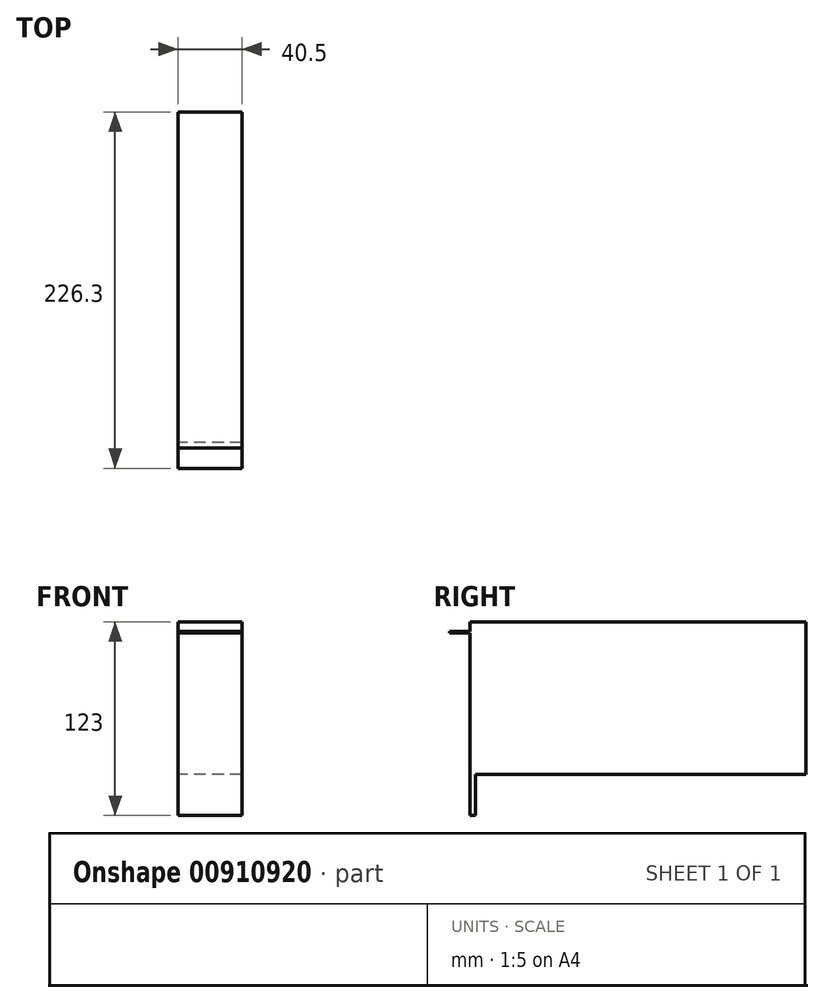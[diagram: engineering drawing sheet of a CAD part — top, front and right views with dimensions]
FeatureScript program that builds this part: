
annotation { "Feature Type Name" : "Feature", "Feature Type Description" : "" }
export const myFeature = defineFeature(function(context is Context, id is Id, definition is map)
    precondition{}
    {
        {
            var Q0;
            Q0=qCreatedBy(makeId("Right.planeOp"),FACE);
            var sketch = newSketch(context, id + "F0", { "sketchPlane" : qUnion([Q0])});
            skLineSegment(sketch, "E0.bottom", {"start": v(-102.54, 35.35) * mm, "end": v(-115.54, 35.35) * mm});
            skLineSegment(sketch, "E0.top", {"start": v(-102.54, 36.35) * mm, "end": v(-115.54, 36.35) * mm});
            skLineSegment(sketch, "E0.left", {"start": v(-102.54, 35.35) * mm, "end": v(-102.54, 36.35) * mm});
            skLineSegment(sketch, "E0.right", {"start": v(-115.54, 35.35) * mm, "end": v(-115.54, 36.35) * mm});
            skLineSegment(sketch, "E1", {"start": v(-102.54, -80.65) * mm, "end": v(-102.54, 35.35) * mm});
            skLineSegment(sketch, "E2", {"start": v(-102.54, -80.65) * mm, "end": v(-99.24, -80.65) * mm});
            skLineSegment(sketch, "E3", {"start": v(-99.24, -80.65) * mm, "end": v(-99.24, -54.65) * mm});
            skLineSegment(sketch, "E4", {"start": v(-99.24, -54.65) * mm, "end": v(110.76, -54.65) * mm});
            skLineSegment(sketch, "E5", {"start": v(110.76, -54.65) * mm, "end": v(110.76, 42.35) * mm});
            skLineSegment(sketch, "E6", {"start": v(110.76, 42.35) * mm, "end": v(-102.54, 42.35) * mm});
            skLineSegment(sketch, "E7", {"start": v(-102.54, 42.35) * mm, "end": v(-102.54, 36.35) * mm});
            skSolve(sketch);
        }
        {
            var Q0;
            Q0 = qSketchRegion(id + "F0", true);
            extrude(context, id + "F1", {"entities" : qUnion([Q0]), "depth" : 40.5 * mm, "offsetDistance" : 25 * mm});
        }
    });
